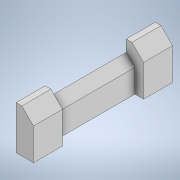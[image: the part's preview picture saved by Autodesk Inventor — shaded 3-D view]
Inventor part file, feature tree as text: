
AUTODESK INVENTOR PART (.ipt)
format: ipt  version: 2021 (Build 250183000, 183)  size: 122,368 bytes
history: native  units: in
note: dims shown in document units (in); Inventor stores cm internally (conversion verified against a paired STEP export)
features: extrude x3, sketch x3
ambient origin geometry x8: Origin, YZ Plane, XZ Plane, XY Plane, X Axis, Y Axis, Z Axis, Center Point
bodies: Solid1 (feature_tree)
feature tree (6):
  extrude  "Extrusion1"  Depth=0.5906in
  extrude  "Extrusion2"  Depth=0.4331in
  extrude  "Extrusion3"  Depth=1.1024in TaperAngle=0.0deg
  sketch  "Sketch1"  dims[d0=0.5906in d1=0.0787in]
  sketch  "Sketch2"  dims[d2=0.2362in d3=0.4331in]
  sketch  "Sketch3"  dims[d4=0.3937in d5=0.0in d7=1.1024in d8=0.0in d9=0.3937in d10=0.0in d13=0.0197in d14=0.0344in d15=0.0197in d16=0.0344in]
